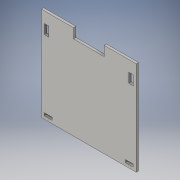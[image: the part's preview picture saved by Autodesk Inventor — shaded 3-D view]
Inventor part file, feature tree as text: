
AUTODESK INVENTOR PART (.ipt)
format: ipt  version: 2016 (Build 200138000, 138)  size: 116,736 bytes
history: native  units: in
note: dims shown in document units (in); Inventor stores cm internally (conversion verified against a paired STEP export)
features: extrude x1, sketch x1
ambient origin geometry x8: Origin, YZ Plane, XZ Plane, XY Plane, X Axis, Y Axis, Z Axis, Center Point
bodies: Body1 (feature_tree)
feature tree (2):
  extrude  "Extrusion3"  Depth=3.88in
  sketch  "Sketch1"  dims[d0=3.92in d1=3.88in d2=1.33in d3=0.4in d4=1.26in d9=0.187in d10=0.395in d12=0.1256in d13=0.187in d14=0.395in d23=0.32in d25=0.11in d27=0.1in d28=0.0in]
